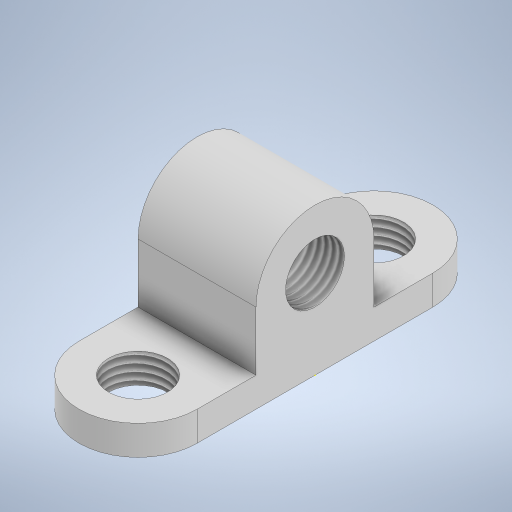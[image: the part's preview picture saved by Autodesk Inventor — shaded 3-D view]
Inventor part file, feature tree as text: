
AUTODESK INVENTOR PART (.ipt)
format: ipt  version: 2024 (Build 280153000, 153)  size: 289,280 bytes
history: native  units: mm
features: thread x3, sketch x3, extrude x2
ambient origin geometry x8: Origin, YZ Plane, XZ Plane, XY Plane, X Axis, Y Axis, Z Axis, Center Point
bodies: Solid1 (feature_tree)
feature tree (8):
  extrude  "Extrusion1"  Depth=10.0mm TaperAngle=0.0deg
  extrude  "Extrusion2"  Depth=10.0mm TaperAngle=0.0deg
  thread  "Thread1"  [1 undecoded]
  thread  "Thread2"  [1 undecoded]
  thread  "Thread3"  [1 undecoded]
  sketch  "Sketch3"
  sketch  "Sketch1"  dims[d8=20.0mm d9=10.0mm d10=0.0mm]
  sketch  "Sketch2"  dims[d14=40.0mm d15=0.0mm d16=10.0mm d17=0.0mm d18=10.0mm d19=0.0mm d20=40.0mm d21=0.0mm]
note: 3 required parameter values undecoded (feature->parameter linkage not recoverable at this tier; creation-order binding heuristic only, values carry confidence <= 0.55)
